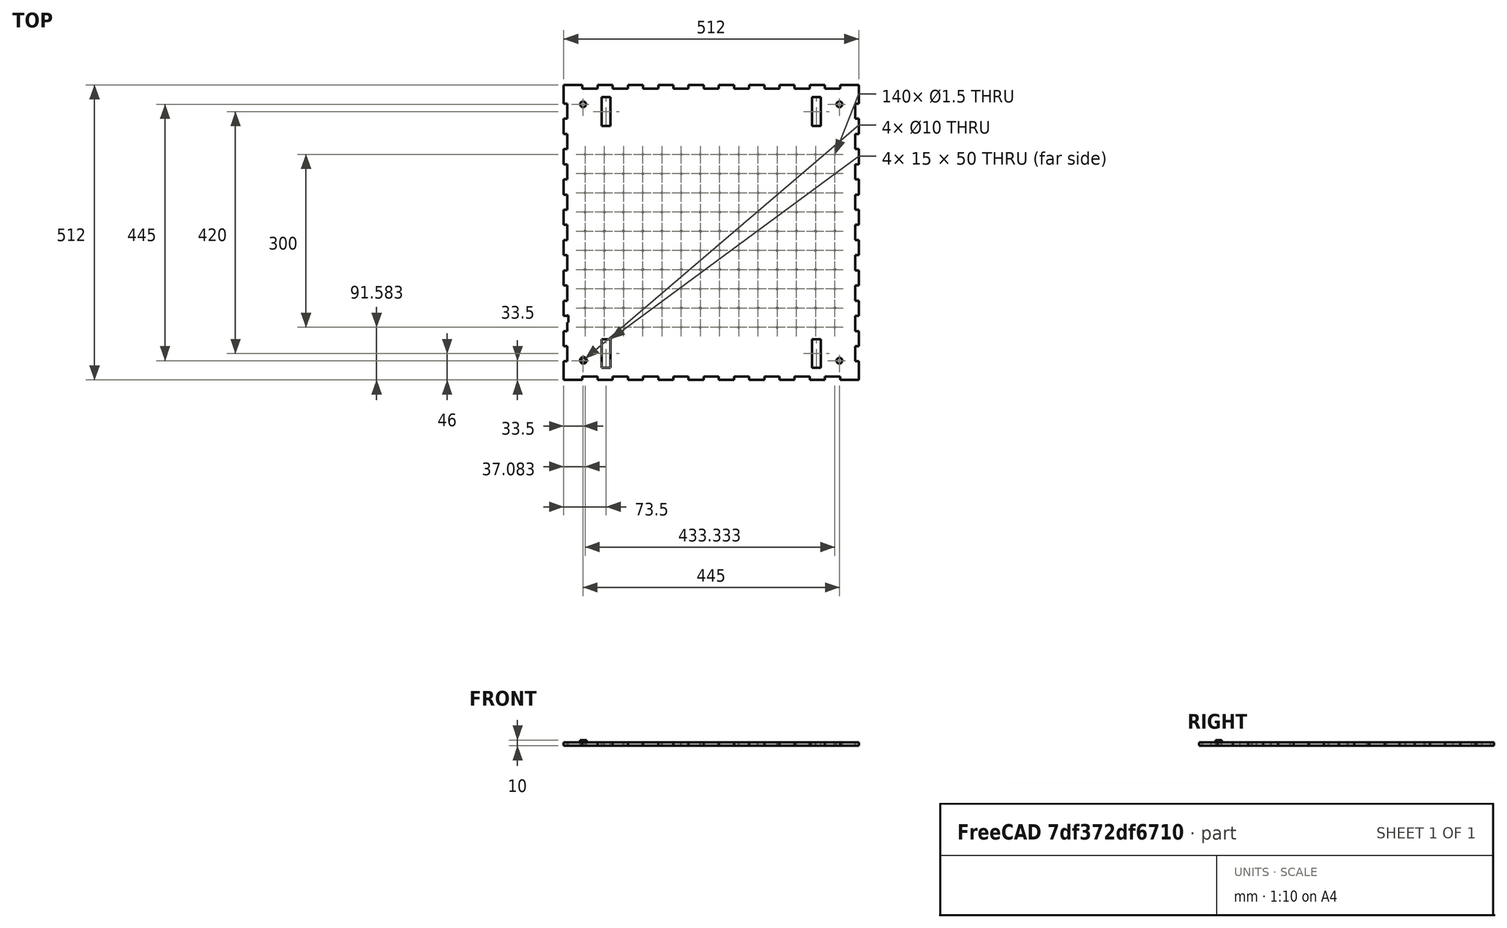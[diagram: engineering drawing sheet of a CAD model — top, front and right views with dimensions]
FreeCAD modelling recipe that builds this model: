
FCSTD DOCUMENT  (FreeCAD 0.16R6527 (Git))
Label: bottom
License: CC-BY 3.0
LicenseURL: http://creativecommons.org/licenses/by/3.0/
objects: Part::FeaturePython×6, Part::Box×5, Part::Cut×4, App::MeasureDistance×2, Part::Cylinder×2, Part::Fuse×2
note: 19 computed .brp shape members not serialized (recipe doc carries the construction recipe); baked Part::Feature solids carry a one-line shape summary decoded from their .brp

FEATURE [Part::Box] Box  label="Slab"
  Height = 6
  Length = 512
  Width = 512
  expr: Width = Slab.Length
  expr: Length = 500mm + 2 * Slab.Height
FEATURE [Part::Box] Box001  label="Horizontal_hole"
  Height = 10
  Length = 26.3158
  Placement = pos=(32.3158,0,0) rot=(0,0,1;0rad)
  Width = 6
  expr: Length = (Slab.Length - 2 * Slab.Height) / 19
  expr: Width = Slab.Height
  expr: Placement.Base.x = Horizontal_hole.Length + Slab.Height
FEATURE [Part::FeaturePython] Array  label="Horizontal_array"  # Draft array (typed FeaturePython)
  Angle = 360
  ArrayType = 0
  Axis = (0,0,1)
  Base = -> Box001
  Center = (0,0,0)
  IntervalX = (52.6316,0,0)
  IntervalY = (0,506,0)
  IntervalZ = (0,0,1)
  NumberPolar = 1
  NumberX = 9
  NumberY = 2
  NumberZ = 0
  expr: IntervalX.x = 2 * Horizontal_hole.Length / 1mm
  expr: IntervalY.y = (Slab.Width - Slab.Height) / 1mm
FEATURE [Part::Box] Box002  label="Vertical_hole"
  Height = 10
  Length = 6
  Placement = pos=(0,32.3158,0) rot=(0,0,1;0rad)
  Width = 26.3158
  expr: Placement.Base.y = Vertical_hole.Width + Slab.Height
  expr: Length = Slab.Height
  expr: Width = (Slab.Width - 2 * Slab.Height) / 19
FEATURE [Part::FeaturePython] Array001  label="Vertical_array"  # Draft array (typed FeaturePython)
  Angle = 360
  ArrayType = 0
  Axis = (0,0,1)
  Base = -> Box002
  Center = (0,0,0)
  Fuse = false
  IntervalAxis = (0,0,0)
  IntervalX = (506,0,0)
  IntervalY = (0,52.6316,0)
  IntervalZ = (0,0,0)
  NumberPolar = 1
  NumberX = 2
  NumberY = 9
  NumberZ = 1
  expr: IntervalX.x = Slab.Length - Slab.Height
  expr: IntervalY.z = 0
  expr: IntervalY.y = 2 * Vertical_hole.Width
FEATURE [Part::Cut] Cut  label="Horizontal_cut"
  Base = -> Box
  Tool = -> Array
FEATURE [Part::Cut] Cut001  label="ToothedSlab"
  Base = -> Cut
  Tool = -> Array001
FEATURE [App::MeasureDistance] Distance001  label="Distance: 333,333 mm"
  Distance = 333.333
  P1 = (58.55,336.333,3)
  P2 = (58.7489,3,3)
FEATURE [App::MeasureDistance] Distance  label="Distance: 500 mm"
  Distance = 500
  P1 = (3,271.467,3)
  P2 = (503,271.467,3)
FEATURE [Part::Box] Box003  label="LineIn_hole"
  Height = 10
  Length = 2
  Placement = pos=(6,100,0) rot=(0,0,1;0rad)
  Width = 12
  expr: Placement.Base.x = Slab.Height
  expr: Placement.Base.y = Slab.Height + (Slab.Width - 2 * Slab.Height - 1000mm / 3 + 100mm / 3 - LineIn_hole.Width) / 2
FEATURE [Part::Box] Box004  label="Trapdoor"
  Height = 10
  Length = 15
  Placement = pos=(66,21,0) rot=(0,0,1;0rad)
  Width = 50
  expr: Placement.Base.y = Slab.Height + 15mm
  expr: Placement.Base.x = Slab.Height + 60mm
FEATURE [Part::FeaturePython] Array003  label="Trapdoors"  # Draft array (typed FeaturePython)
  Angle = 360
  ArrayType = 0
  Axis = (0,0,1)
  Base = -> Box004
  Center = (0,0,0)
  Fuse = false
  IntervalAxis = (0,0,0)
  IntervalX = (365,0,0)
  IntervalY = (0,420,0)
  IntervalZ = (0,0,0)
  NumberPolar = 1
  NumberX = 2
  NumberY = 2
  NumberZ = 1
  expr: IntervalY.y = Slab.Width - 2 * Trapdoor.Placement.Base.y * 1mm - Trapdoor.Width
  expr: IntervalX.x = Slab.Length - 2 * Trapdoor.Placement.Base.x * 1mm - Trapdoor.Length
FEATURE [Part::Cylinder] Cylinder  label="TouchWire"
  Angle = 360
  Height = 10
  Placement = pos=(37.0833,91.5833,0) rot=(0,0,1;0rad)
  Radius = 0.75
  expr: Placement.Base.x = Slab.Height + 100mm / 3 - strip_500#Strip.Width / 2 - TouchWire.Radius
  expr: Placement.Base.y = (Slab.Width - 1000mm / 3) / 2 + strip_500#Strip.Width / 2 + TouchWire.Radius
FEATURE [Part::FeaturePython] Array005  label="TouchWires"  # Draft array (typed FeaturePython)
  Angle = 360
  ArrayType = 0
  Axis = (0,0,1)
  Base = -> Cylinder
  Center = (0,0,0)
  Fuse = false
  IntervalAxis = (0,0,0)
  IntervalX = (33.3333,0,0)
  IntervalY = (0,33.3333,0)
  IntervalZ = (0,0,0)
  NumberPolar = 1
  NumberX = 14
  NumberY = 10
  NumberZ = 1
  expr: IntervalY.y = 100 / 3
  expr: IntervalX.x = 100 / 3
FEATURE [Part::Fuse] Fusion
  Base = -> Box003
  Tool = -> Array003
FEATURE [Part::Fuse] Fusion001  label="CablePassing"
  Base = -> Array005
  Tool = -> Fusion
FEATURE [Part::Cut] Cut002  label="FlatHost"
  Base = -> Cut001
  Tool = -> Fusion001
FEATURE [Part::Cylinder] Cylinder001  label="LegHole"
  Angle = 360
  Height = 10
  Placement = pos=(33.5,33.5,0) rot=(0,0,1;1.30992rad)
  Radius = 5
  expr: Radius = leg#ScrewHole.Radius
  expr: Placement.Base.y = Slab.Height + leg#Cube.Width / 2 + 5mm
  expr: Placement.Base.x = Slab.Height + leg#Cube.Length / 2 + 5mm
FEATURE [Part::FeaturePython] Array006  # Draft array (typed FeaturePython)
  Angle = 360
  ArrayType = 0
  Axis = (0,0,1)
  Base = -> Cylinder001
  Center = (0,0,0)
  Fuse = false
  IntervalAxis = (0,0,0)
  IntervalX = (1,0,0)
  IntervalY = (0,1,0)
  IntervalZ = (0,0,0)
  NumberPolar = 1
  NumberX = 2
  NumberY = 2
  NumberZ = 1
FEATURE [Part::FeaturePython] Array007  label="LegHoles"  # Draft array (typed FeaturePython)
  Angle = 360
  ArrayType = 0
  Axis = (0,0,1)
  Base = -> Cylinder001
  Center = (0,0,0)
  Fuse = false
  IntervalAxis = (0,0,0)
  IntervalX = (445,0,0)
  IntervalY = (0,445,0)
  IntervalZ = (0,0,0)
  NumberPolar = 1
  NumberX = 2
  NumberY = 2
  NumberZ = 1
  expr: IntervalY.y = Slab.Width - 2 * LegHole.Placement.Base.y * 1mm
  expr: IntervalX.x = Slab.Length - 2 * LegHole.Placement.Base.x * 1mm
FEATURE [Part::Cut] Cut003  label="SlabWithLegHoles"
  Base = -> Cut002
  Tool = -> Array007
